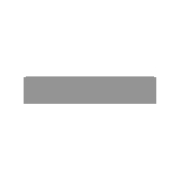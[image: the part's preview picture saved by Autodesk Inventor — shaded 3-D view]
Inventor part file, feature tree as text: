
AUTODESK INVENTOR PART (.ipt)
format: ipt  version: 2019 (Build 230136000, 136)  size: 116,736 bytes
history: native  units: mm
features: other x10, sketch x3, extrude x1
ambient origin geometry x8: Origin, YZ Plane, XZ Plane, XY Plane, X Axis, Y Axis, Z Axis, Center Point
bodies: Body1 (feature_tree)
feature tree (14):
  other  "Контрольная длина"
  other  "Генератор рам"
  other  "Твердое тело1"
  other  "Начальная плоскость"
  other  "Конечная плоскость"
  extrude  "Тело"  [1 undecoded]
  other  "РабПлоскость6"
  other  "Разделение1"
  other  "РабПлоскость7"
  other  "Разделение2"
  sketch  "Эскиз"
  sketch  "Эскиз6"
  other  "РабПлоскость5"
  sketch  "Эскиз7"
note: 1 required parameter value undecoded (feature->parameter linkage not recoverable at this tier; creation-order binding heuristic only, values carry confidence <= 0.55)
